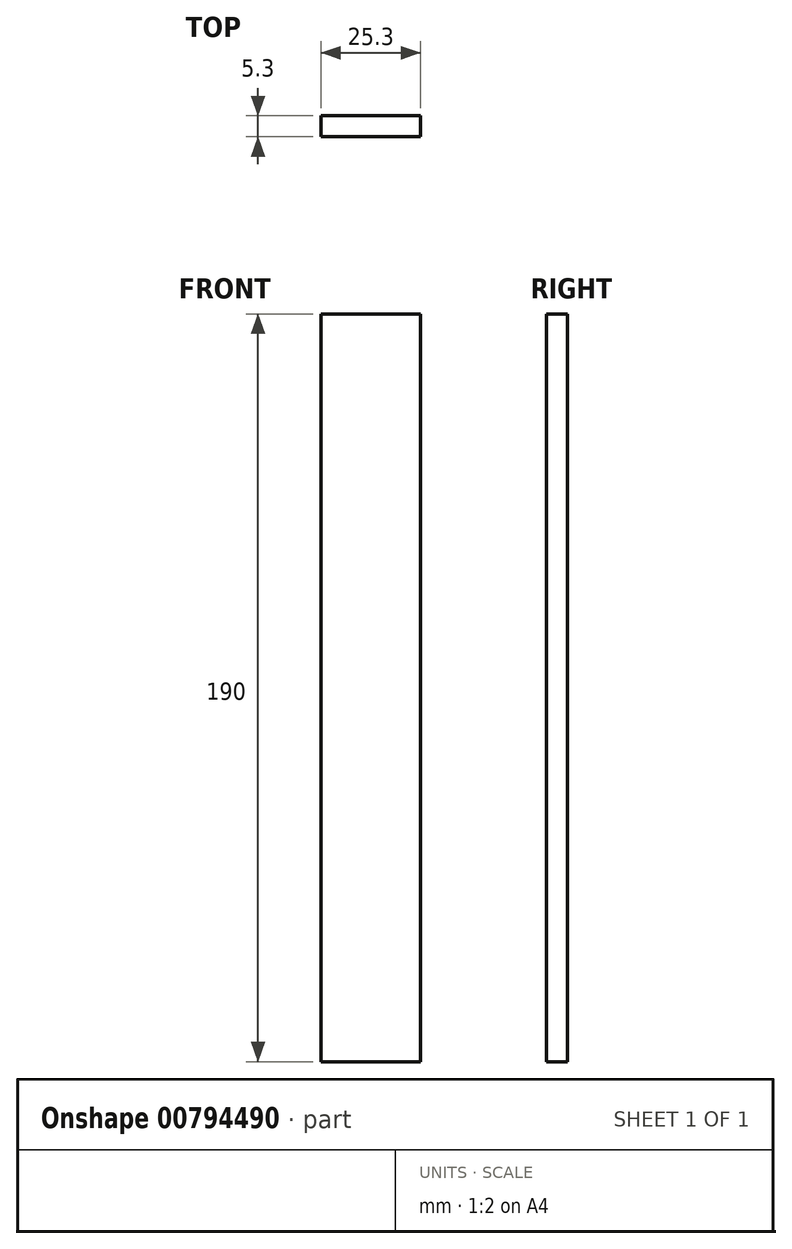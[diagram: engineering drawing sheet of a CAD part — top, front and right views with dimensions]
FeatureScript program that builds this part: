
annotation { "Feature Type Name" : "Feature", "Feature Type Description" : "" }
export const myFeature = defineFeature(function(context is Context, id is Id, definition is map)
    precondition{}
    {
        {
            var Q0;
            Q0=qCreatedBy(makeId("Front.planeOp"),FACE);
            var sketch = newSketch(context, id + "F0", { "sketchPlane" : qUnion([Q0])});
            skLineSegment(sketch, "E0.bottom", {"start": v(-43.31, 46.54) * mm, "end": v(-18.01, 46.54) * mm});
            skLineSegment(sketch, "E0.top", {"start": v(-43.31, -143.46) * mm, "end": v(-18.01, -143.46) * mm});
            skLineSegment(sketch, "E0.left", {"start": v(-43.31, 46.54) * mm, "end": v(-43.31, -143.46) * mm});
            skLineSegment(sketch, "E0.right", {"start": v(-18.01, 46.54) * mm, "end": v(-18.01, -143.46) * mm});
            skSolve(sketch);
        }
        {
            var Q0;
            Q0 = qSketchRegion(id + "F0", true);
            extrude(context, id + "F1", {"entities" : qUnion([Q0]), "depth" : 5.3 * mm, "offsetDistance" : 25 * mm});
        }
    });
